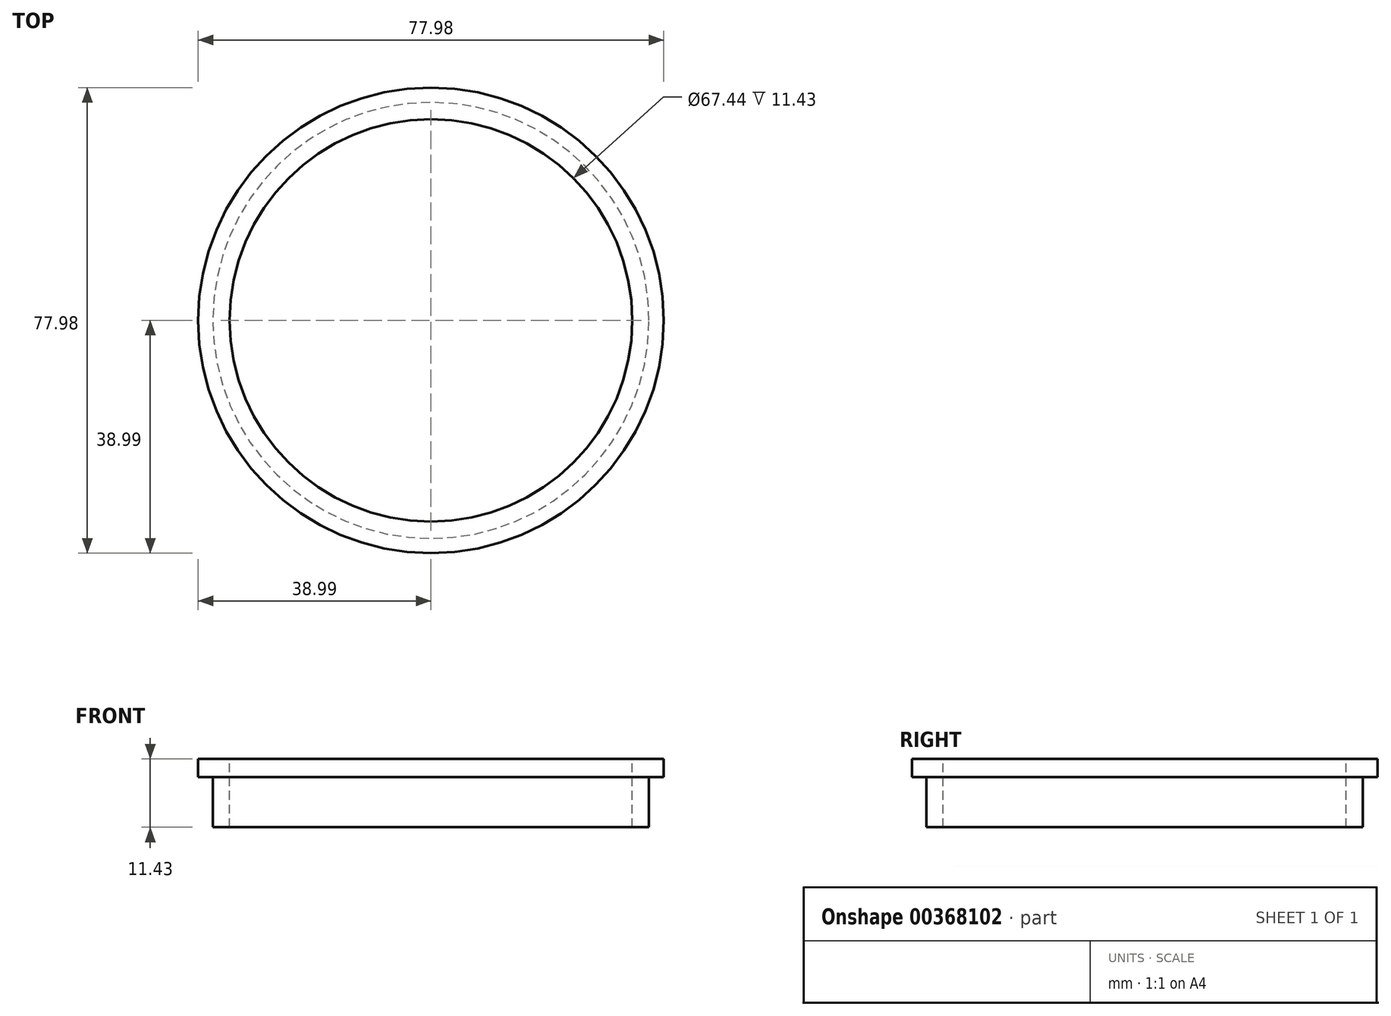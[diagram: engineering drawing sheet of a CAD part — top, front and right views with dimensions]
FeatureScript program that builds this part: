
annotation { "Feature Type Name" : "Feature", "Feature Type Description" : "" }
export const myFeature = defineFeature(function(context is Context, id is Id, definition is map)
    precondition{}
    {
        {
            var Q0;
            Q0=qCreatedBy(makeId("Top.planeOp"),FACE);
            var sketch = newSketch(context, id + "F0", { "sketchPlane" : qUnion([Q0])});
            skCircle(sketch, "E0", {"center": v(0, 0) * mm, "radius": 33.72 * mm});
            skCircle(sketch, "E1", {"center": v(0, 0) * mm, "radius": 36.53 * mm});
            skCircle(sketch, "E2", {"center": v(0, 0) * mm, "radius": 38.99 * mm});
            skLineSegment(sketch, "E3", {"start": v(0, 33.72) * mm, "end": v(0, -33.72) * mm, "construction": true});
            skSolve(sketch);
        }
        {
            var Q0;
            Q0=makeQuery(id+"F0.imprint","IMPRINT",FACE,{"disambiguationData":[TD([[makeQuery(id+"F0.imprint","IMPRINT",EDGE,{"derivedFrom":sQuery(id+"F0.wireOp",EDGE,"E0")}),-1.0]])]});
            extrude(context, id + "F1", {"entities" : qUnion([Q0]), "oppositeDirection" : true, "depth" : 11.43 * mm});
        }
        {
            var Q0;
            Q0 = qSketchRegion(id + "F0", true);
            extrude(context, id + "F2", {"entities" : qUnion([Q0]), "operationType" : NewBodyOperationType.ADD, "oppositeDirection" : true, "depth" : 3.05 * mm});
        }
    });
